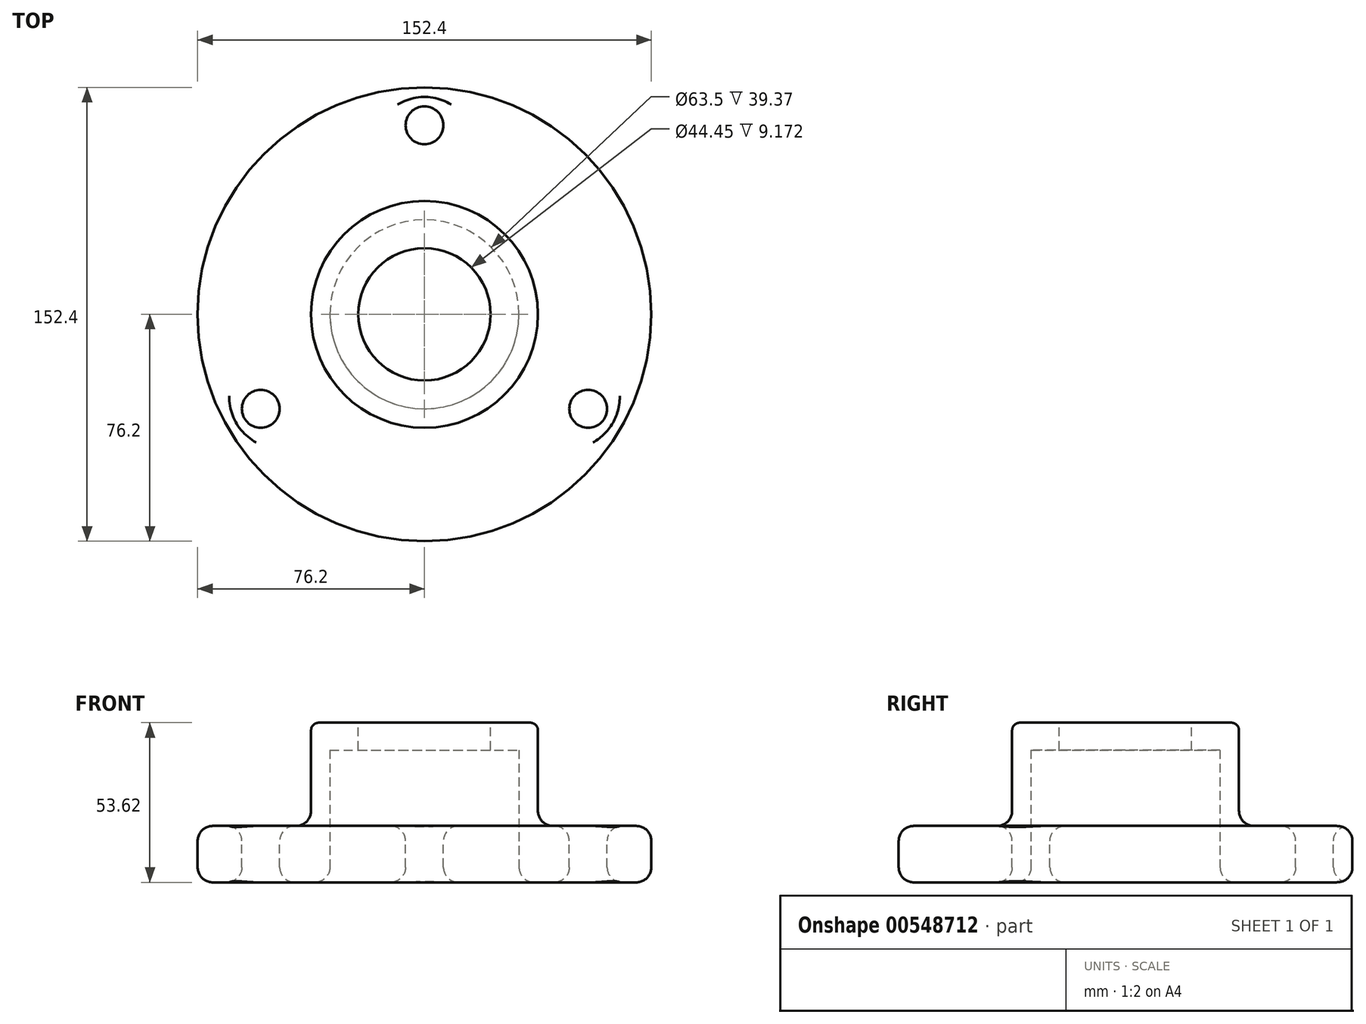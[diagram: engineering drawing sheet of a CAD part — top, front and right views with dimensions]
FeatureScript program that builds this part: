
annotation { "Feature Type Name" : "Feature", "Feature Type Description" : "" }
export const myFeature = defineFeature(function(context is Context, id is Id, definition is map)
    precondition{}
    {
        {
            var Q0;
            Q0=qCreatedBy(makeId("Front.planeOp"),FACE);
            var sketch = newSketch(context, id + "F0", { "sketchPlane" : qUnion([Q0])});
            skLineSegment(sketch, "E0.bottom", {"start": v(0, 0) * mm, "end": v(-76.2, 0) * mm});
            skLineSegment(sketch, "E0.top", {"start": v(0, 18.95) * mm, "end": v(-76.2, 18.95) * mm});
            skLineSegment(sketch, "E0.left", {"start": v(0, 0) * mm, "end": v(0, 18.95) * mm});
            skLineSegment(sketch, "E0.right", {"start": v(-76.2, 0) * mm, "end": v(-76.2, 18.95) * mm});
            skLineSegment(sketch, "E1.bottom", {"start": v(-38.1, 53.62) * mm, "end": v(0, 53.62) * mm});
            skLineSegment(sketch, "E1.top", {"start": v(-38.1, 18.95) * mm, "end": v(0, 18.95) * mm});
            skLineSegment(sketch, "E1.left", {"start": v(-38.1, 53.62) * mm, "end": v(-38.1, 18.95) * mm});
            skLineSegment(sketch, "E1.right", {"start": v(0, 53.62) * mm, "end": v(0, 18.95) * mm});
            skSolve(sketch);
        }
        {
            var Q0;
            Q0 = qSketchRegion(id + "F0", true);
            var Q1;
            Q1=makeQuery(id+"F0.imprint","IMPRINT",FACE,{"disambiguationData":[TD([[makeQuery(id+"F0.imprint","IMPRINT",EDGE,{"derivedFrom":sQuery(id+"F0.wireOp",EDGE,"E1.bottom")}),-1.0]])]});
            var Q2;
            Q2=sQuery(id+"F0.wireOp",EDGE,"E1.right");
            revolve(context, id + "F1", {"entities" : qUnion([Q0, Q1]), "axis" : qUnion([Q2]), "revolveType" : RevolveType.FULL});
        }
        {
            var Q0;
            Q0=makeQuery(id+"F1.opRevolve","SWEPT_FACE",FACE,{"disambiguationData":[OSD([sQuery(id+"F0.wireOp",EDGE,"E0.top")])]});
            var sketch = newSketch(context, id + "F2", { "sketchPlane" : qUnion([Q0])});
            skCircle(sketch, "E2", {"center": v(0, 63.5) * mm, "radius": 6.35 * mm});
            skCircle(sketch, "E3.1.0", {"center": v(-55, -31.75) * mm, "radius": 6.35 * mm});
            skCircle(sketch, "E3.2.0", {"center": v(55, -31.75) * mm, "radius": 6.35 * mm});
            skPoint(sketch, "E3.center", {"position": v(0, 0) * mm});
            skSolve(sketch);
        }
        {
            var Q0;
            Q0=makeQuery(id+"F2.imprint","IMPRINT",FACE,{"disambiguationData":[TD([[makeQuery(id+"F2.imprint","IMPRINT",EDGE,{"derivedFrom":sQuery(id+"F2.wireOp",EDGE,"E3.1.0")}),1.0]])]});
            var Q1;
            Q1=makeQuery(id+"F2.imprint","IMPRINT",FACE,{"disambiguationData":[TD([[makeQuery(id+"F2.imprint","IMPRINT",EDGE,{"derivedFrom":sQuery(id+"F2.wireOp",EDGE,"E3.2.0")}),1.0]])]});
            var Q2;
            Q2=makeQuery(id+"F2.imprint","IMPRINT",FACE,{"disambiguationData":[TD([[makeQuery(id+"F2.imprint","IMPRINT",EDGE,{"derivedFrom":sQuery(id+"F2.wireOp",EDGE,"E2")}),1.0]])]});
            extrude(context, id + "F3", {"entities" : qUnion([Q0, Q1, Q2]), "operationType" : NewBodyOperationType.REMOVE, "endBound" : BoundingType.THROUGH_ALL, "oppositeDirection" : true, "depth" : 25.4 * mm, "offsetDistance" : 25.4 * mm});
        }
        {
            var Q0;
            Q0=makeQuery(id+"F1.opRevolve","SWEPT_FACE",FACE,{"disambiguationData":[OSD([sQuery(id+"F0.wireOp",EDGE,"E0.bottom")])]});
            var sketch = newSketch(context, id + "F4", { "sketchPlane" : qUnion([Q0])});
            skCircle(sketch, "E4", {"center": v(0, 0) * mm, "radius": 31.75 * mm});
            skSolve(sketch);
        }
        {
            var Q0;
            Q0=makeQuery(id+"F4.imprint","IMPRINT",FACE,{"disambiguationData":[TD([[makeQuery(id+"F4.imprint","IMPRINT",EDGE,{"derivedFrom":sQuery(id+"F4.wireOp",EDGE,"E4")}),1.0]])]});
            extrude(context, id + "F5", {"entities" : qUnion([Q0]), "operationType" : NewBodyOperationType.REMOVE, "oppositeDirection" : true, "depth" : 44.45 * mm, "offsetDistance" : 25.4 * mm});
        }
        {
            var Q0;
            Q0=makeQuery(id+"F1.opRevolve","SWEPT_FACE",FACE,{"disambiguationData":[OSD([sQuery(id+"F0.wireOp",EDGE,"E1.bottom")])]});
            var sketch = newSketch(context, id + "F6", { "sketchPlane" : qUnion([Q0])});
            skCircle(sketch, "E5", {"center": v(0, 0) * mm, "radius": 22.23 * mm});
            skSolve(sketch);
        }
        {
            var Q0;
            Q0=makeQuery(id+"F6.imprint","IMPRINT",FACE,{"disambiguationData":[TD([[makeQuery(id+"F6.imprint","IMPRINT",EDGE,{"derivedFrom":sQuery(id+"F6.wireOp",EDGE,"E5")}),1.0]])]});
            extrude(context, id + "F7", {"entities" : qUnion([Q0]), "operationType" : NewBodyOperationType.REMOVE, "oppositeDirection" : true, "depth" : 25.4 * mm, "offsetDistance" : 25.4 * mm});
        }
        {
            var Q0;
            Q0=makeQuery(id+"F1.opRevolve","SWEPT_EDGE",EDGE,{"disambiguationData":[OSD([sQuery(id+"F0.wireOp",EDGE,"E1.bottom"),sQuery(id+"F0.wireOp",EDGE,"E1.left")])]});
            var Q1;
            Q1=makeQuery(id+"F7.boolean.opBoolean","COPY",EDGE,{"derivedFrom":makeQuery(id+"F7.opExtrude","CAP_EDGE",EDGE,{"disambiguationData":[OSD([sQuery(id+"F6.wireOp",EDGE,"E5")])],"isStart":true})});
            fillet(context, id + "F8", {"entities" : qUnion([Q0, Q1]), "radius" : 2.54 * mm, "tangentPropagation" : true, "allowEdgeOverflow" : false});
        }
        {
            var Q0;
            Q0=makeQuery(id+"F1.opRevolve","SWEPT_FACE",FACE,{"disambiguationData":[OSD([sQuery(id+"F0.wireOp",EDGE,"E0.top")])]});
            fillet(context, id + "F9", {"entities" : qUnion([Q0]), "radius" : 5.08 * mm, "tangentPropagation" : true, "allowEdgeOverflow" : false});
        }
        {
            var Q0;
            Q0=makeQuery(id+"F1.opRevolve","SWEPT_FACE",FACE,{"disambiguationData":[OSD([sQuery(id+"F0.wireOp",EDGE,"E0.bottom")])]});
            fillet(context, id + "F10", {"entities" : qUnion([Q0]), "radius" : 5.08 * mm, "tangentPropagation" : true, "allowEdgeOverflow" : false});
        }
    });
